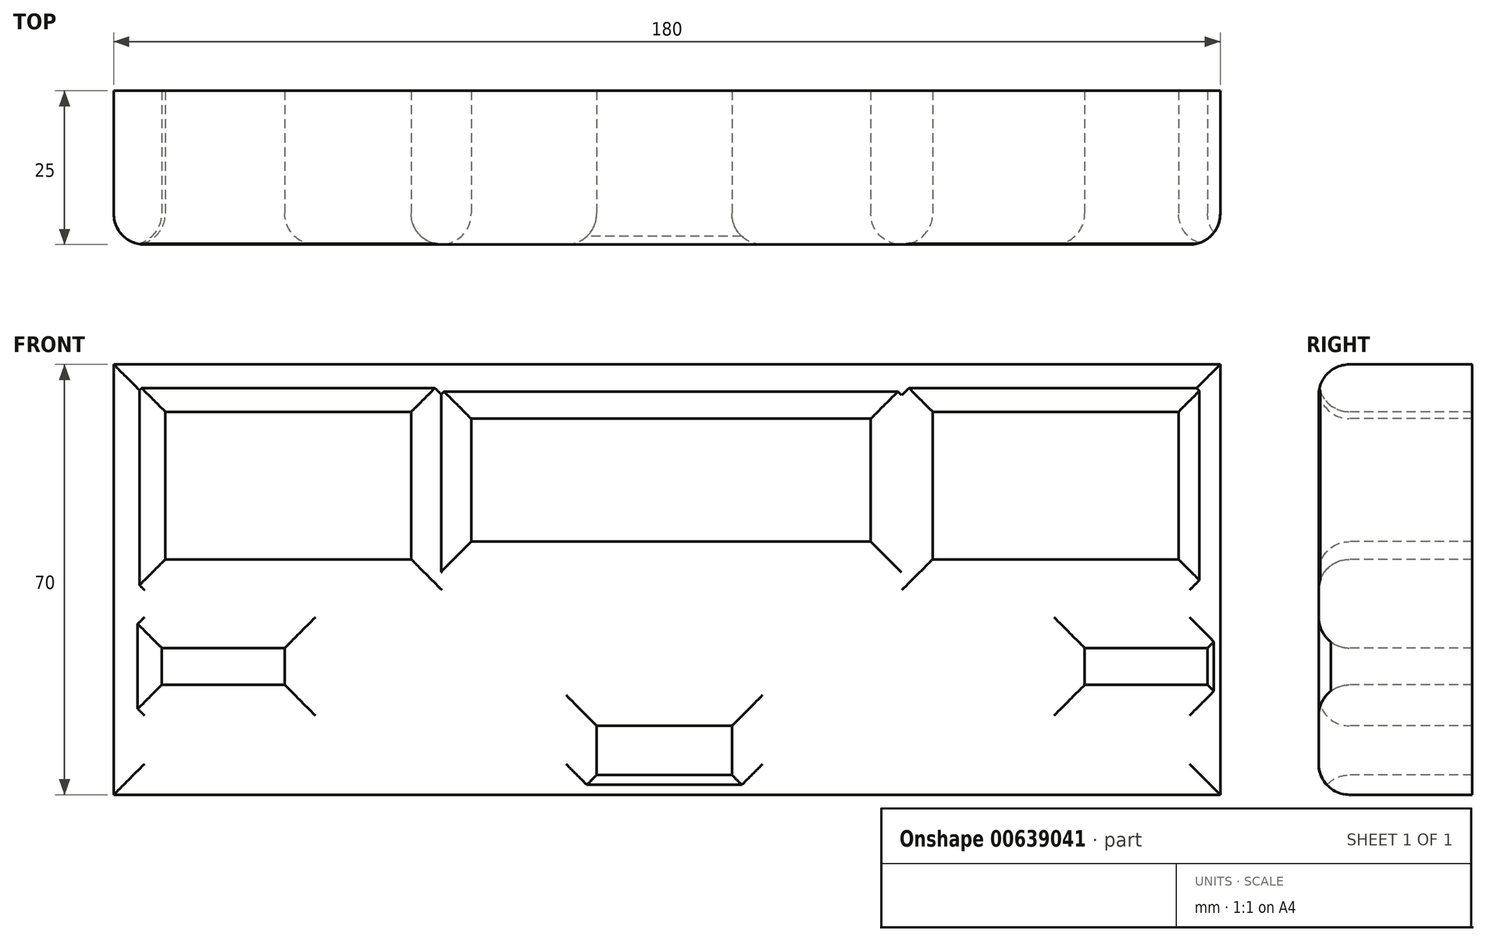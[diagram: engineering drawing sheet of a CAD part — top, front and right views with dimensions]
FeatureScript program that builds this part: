
annotation { "Feature Type Name" : "Feature", "Feature Type Description" : "" }
export const myFeature = defineFeature(function(context is Context, id is Id, definition is map)
    precondition{}
    {
        {
            var Q0;
            Q0=qCreatedBy(makeId("Front.planeOp"),FACE);
            var sketch = newSketch(context, id + "F0", { "sketchPlane" : qUnion([Q0])});
            skLineSegment(sketch, "E0.bottom", {"start": v(90, -35) * mm, "end": v(-90, -35) * mm});
            skLineSegment(sketch, "E0.top", {"start": v(90, 35) * mm, "end": v(-90, 35) * mm});
            skLineSegment(sketch, "E0.left", {"start": v(90, -35) * mm, "end": v(90, 35) * mm});
            skLineSegment(sketch, "E0.right", {"start": v(-90, -35) * mm, "end": v(-90, 35) * mm});
            skPoint(sketch, "E0.middle", {"position": v(0, 0) * mm});
            skSolve(sketch);
        }
        {
            var Q0;
            Q0=makeQuery(id+"F0.imprint","IMPRINT",FACE,{"disambiguationData":[TD([[makeQuery(id+"F0.imprint","IMPRINT",EDGE,{"derivedFrom":sQuery(id+"F0.wireOp",EDGE,"E0.bottom")}),-1.0]])]});
            extrude(context, id + "F1", {"entities" : qUnion([Q0]), "depth" : 25 * mm, "offsetDistance" : 25 * mm});
        }
        {
            var Q0;
            Q0=makeQuery(id+"F1.opExtrude","CAP_FACE",FACE,{"disambiguationData":[OSD([sQuery(id+"F0.wireOp",EDGE,"E0.bottom"),sQuery(id+"F0.wireOp",EDGE,"E0.top"),sQuery(id+"F0.wireOp",EDGE,"E0.left"),sQuery(id+"F0.wireOp",EDGE,"E0.right")])],"isStart":false});
            var sketch = newSketch(context, id + "F2", { "sketchPlane" : qUnion([Q0])});
            skSolve(sketch);
        }
        {
            var Q0;
            Q0=makeQuery(id+"F2.imprint","IMPRINT",FACE,{"disambiguationData":[TD([[makeQuery(id+"F2.imprint","IMPRINT",EDGE,{"derivedFrom":makeQuery(id+"F1.opExtrude","CAP_EDGE",EDGE,{"disambiguationData":[OSD([sQuery(id+"F0.wireOp",EDGE,"E0.bottom")])],"isStart":false})}),-1.0]])]});
            var sketch = newSketch(context, id + "F3", { "sketchPlane" : qUnion([Q0])});
            skLineSegment(sketch, "E1.bottom", {"start": v(-81.61, 27.3) * mm, "end": v(-41.61, 27.3) * mm});
            skLineSegment(sketch, "E1.top", {"start": v(-81.61, 3.3) * mm, "end": v(-41.61, 3.3) * mm});
            skLineSegment(sketch, "E1.left", {"start": v(-81.61, 27.3) * mm, "end": v(-81.61, 3.3) * mm});
            skLineSegment(sketch, "E1.right", {"start": v(-41.61, 27.3) * mm, "end": v(-41.61, 3.3) * mm});
            skLineSegment(sketch, "E2.bottom", {"start": v(83.21, 3.3) * mm, "end": v(43.21, 3.3) * mm});
            skLineSegment(sketch, "E2.top", {"start": v(83.21, 27.3) * mm, "end": v(43.21, 27.3) * mm});
            skLineSegment(sketch, "E2.left", {"start": v(83.21, 3.3) * mm, "end": v(83.21, 27.3) * mm});
            skLineSegment(sketch, "E2.right", {"start": v(43.21, 3.3) * mm, "end": v(43.21, 27.3) * mm});
            skLineSegment(sketch, "E3.bottom", {"start": v(-31.86, 26.17) * mm, "end": v(33.14, 26.17) * mm});
            skLineSegment(sketch, "E3.top", {"start": v(-31.86, 6.17) * mm, "end": v(33.14, 6.17) * mm});
            skLineSegment(sketch, "E3.left", {"start": v(-31.86, 26.17) * mm, "end": v(-31.86, 6.17) * mm});
            skLineSegment(sketch, "E3.right", {"start": v(33.14, 26.17) * mm, "end": v(33.14, 6.17) * mm});
            skLineSegment(sketch, "E4.bottom", {"start": v(-82.19, -11.13) * mm, "end": v(-62.19, -11.13) * mm});
            skLineSegment(sketch, "E4.top", {"start": v(-82.19, -17.13) * mm, "end": v(-62.19, -17.13) * mm});
            skLineSegment(sketch, "E4.left", {"start": v(-82.19, -11.13) * mm, "end": v(-82.19, -17.13) * mm});
            skLineSegment(sketch, "E4.right", {"start": v(-62.19, -11.13) * mm, "end": v(-62.19, -17.13) * mm});
            skLineSegment(sketch, "E5.bottom", {"start": v(87.95, -17.13) * mm, "end": v(67.95, -17.13) * mm});
            skLineSegment(sketch, "E5.top", {"start": v(87.95, -11.13) * mm, "end": v(67.95, -11.13) * mm});
            skLineSegment(sketch, "E5.left", {"start": v(87.95, -17.13) * mm, "end": v(87.95, -11.13) * mm});
            skLineSegment(sketch, "E5.right", {"start": v(67.95, -17.13) * mm, "end": v(67.95, -11.13) * mm});
            skLineSegment(sketch, "E6.bottom", {"start": v(-11.44, -23.8) * mm, "end": v(10.56, -23.8) * mm});
            skLineSegment(sketch, "E6.top", {"start": v(-11.44, -31.8) * mm, "end": v(10.56, -31.8) * mm});
            skLineSegment(sketch, "E6.left", {"start": v(-11.44, -23.8) * mm, "end": v(-11.44, -31.8) * mm});
            skLineSegment(sketch, "E6.right", {"start": v(10.56, -23.8) * mm, "end": v(10.56, -31.8) * mm});
            skSolve(sketch);
        }
        {
            var Q0;
            Q0 = qSketchRegion(id + "F3", true);
            extrude(context, id + "F4", {"entities" : qUnion([Q0]), "operationType" : NewBodyOperationType.REMOVE, "oppositeDirection" : true, "depth" : 40 * mm, "offsetDistance" : 25 * mm});
        }
        {
            var Q0;
            Q0=makeQuery(id+"F1.opExtrude","CAP_FACE",FACE,{"disambiguationData":[OSD([sQuery(id+"F0.wireOp",EDGE,"E0.bottom"),sQuery(id+"F0.wireOp",EDGE,"E0.top"),sQuery(id+"F0.wireOp",EDGE,"E0.left"),sQuery(id+"F0.wireOp",EDGE,"E0.right")])],"isStart":false});
            fillet(context, id + "F5", {"entities" : qUnion([Q0]), "radius" : 5 * mm, "tangentPropagation" : true, "allowEdgeOverflow" : false});
        }
    });
